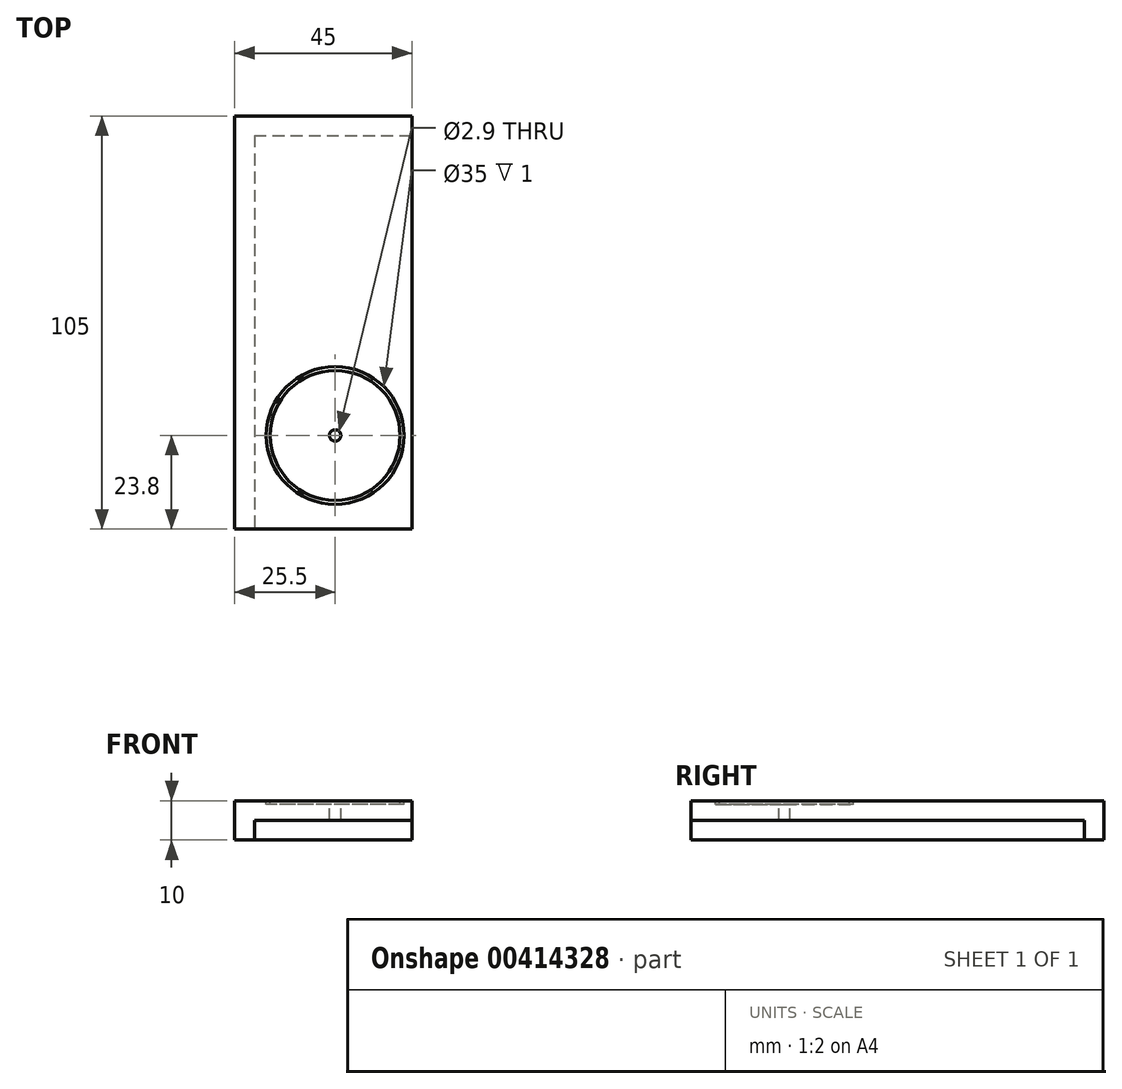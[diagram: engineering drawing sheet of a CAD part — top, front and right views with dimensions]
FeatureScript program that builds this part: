
annotation { "Feature Type Name" : "Feature", "Feature Type Description" : "" }
export const myFeature = defineFeature(function(context is Context, id is Id, definition is map)
    precondition{}
    {
        {
            var Q0;
            Q0=qCreatedBy(makeId("Top.planeOp"),FACE);
            var sketch = newSketch(context, id + "F0", { "sketchPlane" : qUnion([Q0])});
            skLineSegment(sketch, "E0.bottom", {"start": v(-20, 50) * mm, "end": v(20, 50) * mm});
            skLineSegment(sketch, "E0.top", {"start": v(-20, -50) * mm, "end": v(20, -50) * mm});
            skLineSegment(sketch, "E0.left", {"start": v(-20, 50) * mm, "end": v(-20, -50) * mm});
            skLineSegment(sketch, "E0.right", {"start": v(20, 50) * mm, "end": v(20, -50) * mm});
            skPoint(sketch, "E0.middle", {"position": v(0, 0) * mm});
            skCircle(sketch, "E1", {"center": v(0.5, -26.2) * mm, "radius": 17.5 * mm});
            skCircle(sketch, "E2", {"center": v(0.5, -26.2) * mm, "radius": 1.45 * mm});
            skSolve(sketch);
        }
        {
            var Q0;
            Q0=makeQuery(id+"F0.imprint","IMPRINT",FACE,{"disambiguationData":[TD([[makeQuery(id+"F0.imprint","IMPRINT",EDGE,{"derivedFrom":sQuery(id+"F0.wireOp",EDGE,"E0.bottom")}),-1.0]])]});
            var Q1;
            Q1=makeQuery(id+"F0.imprint","IMPRINT",FACE,{"disambiguationData":[TD([[makeQuery(id+"F0.imprint","IMPRINT",EDGE,{"derivedFrom":sQuery(id+"F0.wireOp",EDGE,"E1")}),1.0]])]});
            extrude(context, id + "F1", {"entities" : qUnion([Q0, Q1]), "oppositeDirection" : true, "depth" : 5 * mm});
        }
        {
            var Q0;
            Q0=makeQuery(id+"F0.imprint","IMPRINT",FACE,{"disambiguationData":[TD([[makeQuery(id+"F0.imprint","IMPRINT",EDGE,{"derivedFrom":sQuery(id+"F0.wireOp",EDGE,"E0.bottom")}),-1.0]])]});
            var sketch = newSketch(context, id + "F2", { "sketchPlane" : qUnion([Q0])});
            skLineSegment(sketch, "E3.bottom", {"start": v(-20, -50) * mm, "end": v(-25, -50) * mm});
            skLineSegment(sketch, "E3.top", {"start": v(-20, 50) * mm, "end": v(-25, 50) * mm});
            skLineSegment(sketch, "E3.left", {"start": v(-20, -50) * mm, "end": v(-20, 50) * mm});
            skLineSegment(sketch, "E3.right", {"start": v(-25, -50) * mm, "end": v(-25, 50) * mm});
            skLineSegment(sketch, "E4.bottom", {"start": v(20, 55) * mm, "end": v(-25, 55) * mm});
            skLineSegment(sketch, "E4.top", {"start": v(20, 50) * mm, "end": v(-25, 50) * mm});
            skLineSegment(sketch, "E4.left", {"start": v(20, 55) * mm, "end": v(20, 50) * mm});
            skLineSegment(sketch, "E4.right", {"start": v(-25, 55) * mm, "end": v(-25, 50) * mm});
            skSolve(sketch);
        }
        {
            var Q0;
            Q0=makeQuery(id+"F2.imprint","IMPRINT",FACE,{"disambiguationData":[TD([[makeQuery(id+"F2.imprint","IMPRINT",EDGE,{"derivedFrom":sQuery(id+"F2.wireOp",EDGE,"E3.bottom")}),-1.0]])]});
            var Q1;
            Q1=makeQuery(id+"F2.imprint","IMPRINT",FACE,{"disambiguationData":[TD([[makeQuery(id+"F2.imprint","IMPRINT",EDGE,{"derivedFrom":sQuery(id+"F2.wireOp",EDGE,"E4.bottom")}),1.0]])]});
            extrude(context, id + "F3", {"entities" : qUnion([Q0, Q1]), "operationType" : NewBodyOperationType.ADD, "oppositeDirection" : true, "depth" : 10 * mm});
        }
        {
            var Q0;
            Q0=makeQuery(id+"F3.boolean.opBoolean","MERGE",FACE,{"derivedFrom":[makeQuery(id+"F1.opExtrude","CAP_FACE",FACE,{"disambiguationData":[OSD([sQuery(id+"F0.wireOp",EDGE,"E0.bottom"),sQuery(id+"F0.wireOp",EDGE,"E0.top"),sQuery(id+"F0.wireOp",EDGE,"E0.left"),sQuery(id+"F0.wireOp",EDGE,"E0.right"),sQuery(id+"F0.wireOp",EDGE,"E2")])],"isStart":true}),makeQuery(id+"F3.opExtrude","CAP_FACE",FACE,{"disambiguationData":[OSD([sQuery(id+"F2.wireOp",EDGE,"E3.bottom"),sQuery(id+"F2.wireOp",EDGE,"E3.left"),sQuery(id+"F2.wireOp",EDGE,"E3.right"),sQuery(id+"F2.wireOp",EDGE,"E4.bottom"),sQuery(id+"F2.wireOp",EDGE,"E4.top"),sQuery(id+"F2.wireOp",EDGE,"E4.left"),sQuery(id+"F2.wireOp",EDGE,"E4.right")])],"isStart":true})]});
            var sketch = newSketch(context, id + "F4", { "sketchPlane" : qUnion([Q0])});
            skCircle(sketch, "E5", {"center": v(0.5, -26.2) * mm, "radius": 17.5 * mm});
            skCircle(sketch, "E6", {"center": v(0.5, -26.2) * mm, "radius": 16.5 * mm});
            skSolve(sketch);
        }
        {
            var Q0;
            Q0=makeQuery(id+"F4.imprint","IMPRINT",FACE,{"disambiguationData":[TD([[makeQuery(id+"F4.imprint","IMPRINT",EDGE,{"derivedFrom":sQuery(id+"F4.wireOp",EDGE,"E5")}),1.0]])]});
            extrude(context, id + "F5", {"entities" : qUnion([Q0]), "operationType" : NewBodyOperationType.REMOVE, "oppositeDirection" : true, "depth" : 1 * mm});
        }
    });
